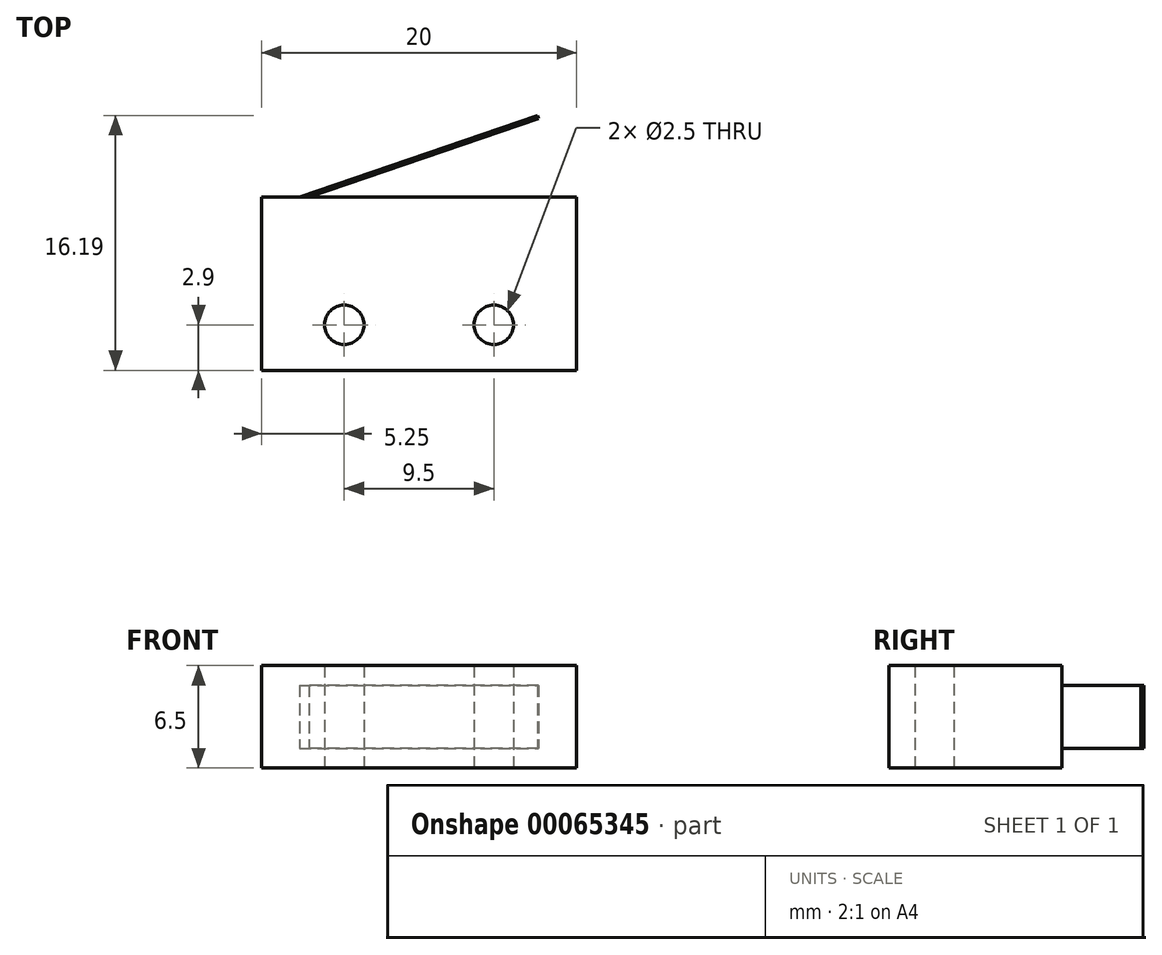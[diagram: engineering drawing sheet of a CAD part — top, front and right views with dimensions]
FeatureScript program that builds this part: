
annotation { "Feature Type Name" : "Feature", "Feature Type Description" : "" }
export const myFeature = defineFeature(function(context is Context, id is Id, definition is map)
    precondition{}
    {
        {
            var Q0;
            Q0=qCreatedBy(makeId("Top.planeOp"),FACE);
            var sketch = newSketch(context, id + "F0", { "sketchPlane" : qUnion([Q0])});
            skLineSegment(sketch, "E0.bottom", {"start": v(0, 0) * mm, "end": v(20, 0) * mm});
            skLineSegment(sketch, "E0.top", {"start": v(0, 11) * mm, "end": v(20, 11) * mm});
            skLineSegment(sketch, "E0.left", {"start": v(0, 0) * mm, "end": v(0, 11) * mm});
            skLineSegment(sketch, "E0.right", {"start": v(20, 0) * mm, "end": v(20, 11) * mm});
            skCircle(sketch, "E1", {"center": v(5.25, 2.9) * mm, "radius": 1.25 * mm});
            skCircle(sketch, "E2", {"center": v(14.75, 2.9) * mm, "radius": 1.25 * mm});
            skLineSegment(sketch, "E3", {"start": v(10, 19.83) * mm, "end": v(10, -14.56) * mm, "construction": true});
            skSolve(sketch);
        }
        {
            var Q0;
            Q0 = qSketchRegion(id + "F0", true);
            extrude(context, id + "F1", {"entities" : qUnion([Q0]), "depth" : 6.5 * mm});
        }
        {
            var Q0;
            Q0=makeQuery(id+"F1.opExtrude","CAP_FACE",FACE,{"disambiguationData":[OSD([sQuery(id+"F0.wireOp",EDGE,"E0.bottom"),sQuery(id+"F0.wireOp",EDGE,"E0.top"),sQuery(id+"F0.wireOp",EDGE,"E0.left"),sQuery(id+"F0.wireOp",EDGE,"E0.right"),sQuery(id+"F0.wireOp",EDGE,"E1"),sQuery(id+"F0.wireOp",EDGE,"E2")])],"isStart":false});
            var Q1;
            Q1=makeQuery(id+"F1.opExtrude","CAP_FACE",FACE,{"disambiguationData":[OSD([sQuery(id+"F0.wireOp",EDGE,"E0.bottom"),sQuery(id+"F0.wireOp",EDGE,"E0.top"),sQuery(id+"F0.wireOp",EDGE,"E0.left"),sQuery(id+"F0.wireOp",EDGE,"E0.right"),sQuery(id+"F0.wireOp",EDGE,"E1"),sQuery(id+"F0.wireOp",EDGE,"E2")])],"isStart":true});
            cPlane(context, id + "F2", {"entities" : qUnion([Q0, Q1]), "cplaneType" : CPlaneType.MID_PLANE, "offset" : 150 * mm, "width" : 150 * mm, "height" : 150 * mm});
        }
        {
            var Q0;
            Q0=qCreatedBy(id+"F2.planeOp",FACE);
            var sketch = newSketch(context, id + "F3", { "sketchPlane" : qUnion([Q0])});
            skLineSegment(sketch, "E4", {"start": v(2.4, 11) * mm, "end": v(17.54, 16.19) * mm});
            skLineSegment(sketch, "E5", {"start": v(17.54, 16.19) * mm, "end": v(17.6, 16) * mm});
            skLineSegment(sketch, "E6", {"start": v(17.6, 16) * mm, "end": v(3.02, 11) * mm});
            skLineSegment(sketch, "E7", {"start": v(2.4, 11) * mm, "end": v(3.02, 11) * mm});
            skSolve(sketch);
        }
        {
            var Q0;
            Q0 = qSketchRegion(id + "F3", true);
            extrude(context, id + "F4", {"entities" : qUnion([Q0]), "operationType" : NewBodyOperationType.ADD, "endBound" : BoundingType.SYMMETRIC, "depth" : 4 * mm});
        }
    });
